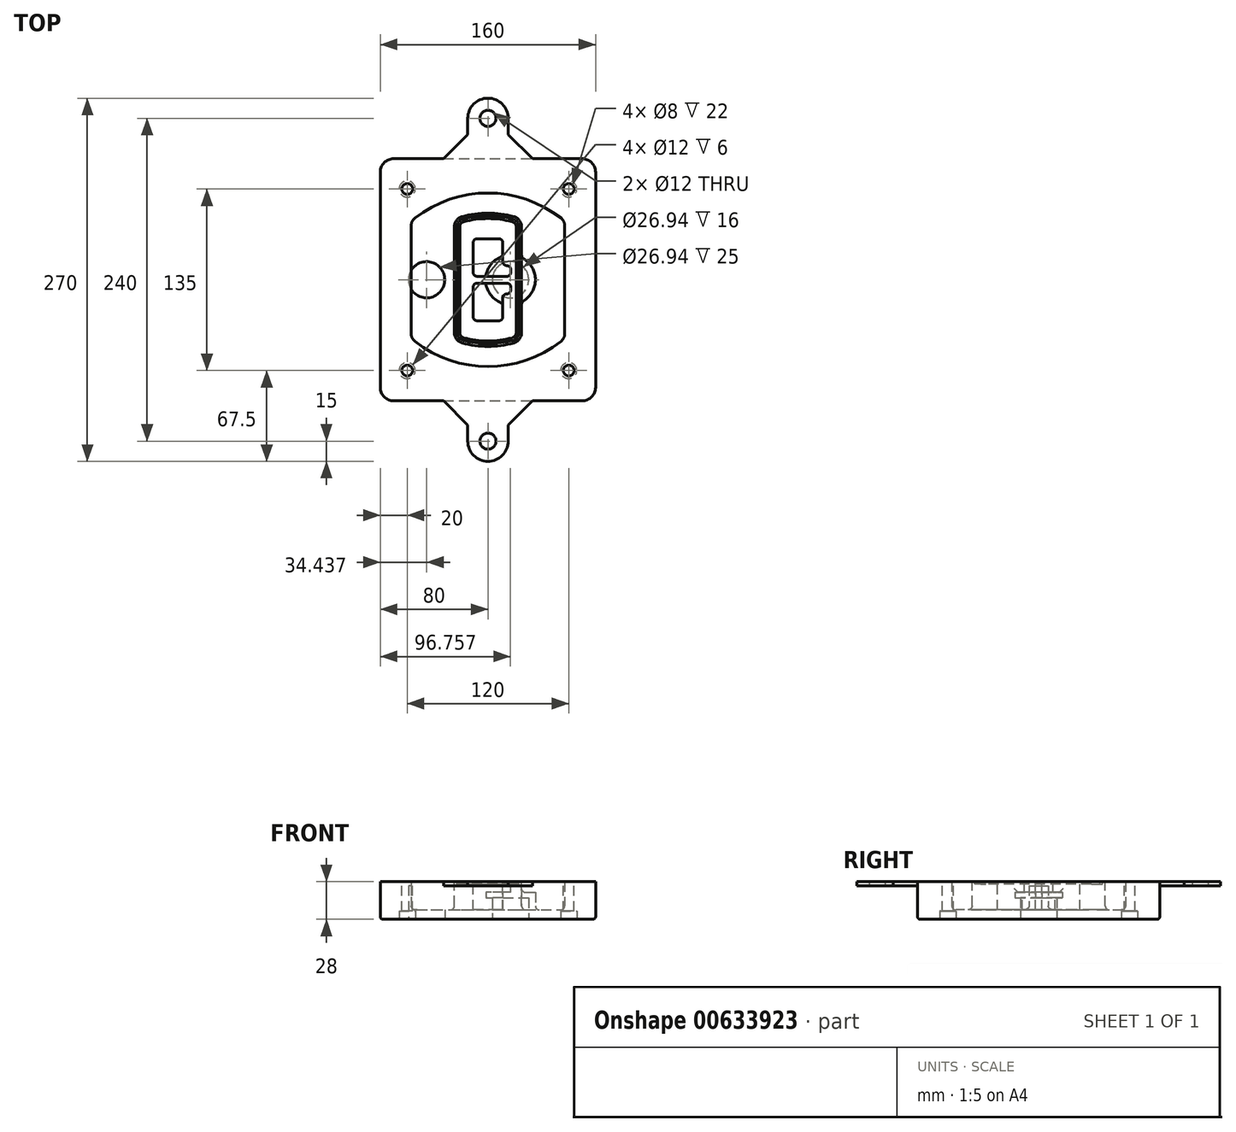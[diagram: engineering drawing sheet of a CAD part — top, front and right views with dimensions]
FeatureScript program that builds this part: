
annotation { "Feature Type Name" : "Feature", "Feature Type Description" : "" }
export const myFeature = defineFeature(function(context is Context, id is Id, definition is map)
    precondition{}
    {
        {
            var Q0;
            Q0=qCreatedBy(makeId("Top.planeOp"),FACE);
            var sketch = newSketch(context, id + "F0", { "sketchPlane" : qUnion([Q0])});
            skPoint(sketch, "E0.rect.middle", {"position": v(0, 0) * mm});
            skLineSegment(sketch, "E1.bottom", {"start": v(-70, -90) * mm, "end": v(70, -90) * mm});
            skLineSegment(sketch, "E1.top", {"start": v(-70, 90) * mm, "end": v(70, 90) * mm});
            skLineSegment(sketch, "E1.left", {"start": v(-80, -80) * mm, "end": v(-80, 80) * mm});
            skLineSegment(sketch, "E1.right", {"start": v(80, -80) * mm, "end": v(80, 80) * mm});
            skLineSegment(sketch, "E2", {"start": v(-80, 90) * mm, "end": v(80, -90) * mm, "construction": true});
            skLineSegment(sketch, "E3", {"start": v(80, 90) * mm, "end": v(-80, -90) * mm, "construction": true});
            skCircle(sketch, "E4", {"center": v(-60, 67.5) * mm, "radius": 4 * mm});
            skCircle(sketch, "E5", {"center": v(60, 67.5) * mm, "radius": 4 * mm});
            skCircle(sketch, "E6", {"center": v(60, -67.5) * mm, "radius": 4 * mm});
            skCircle(sketch, "E7", {"center": v(-60, -67.5) * mm, "radius": 4 * mm});
            skLineSegment(sketch, "E8", {"start": v(-60, 67.5) * mm, "end": v(60, 67.5) * mm, "construction": true});
            skLineSegment(sketch, "E9", {"start": v(60, 67.5) * mm, "end": v(60, -67.5) * mm, "construction": true});
            skLineSegment(sketch, "E10", {"start": v(60, -67.5) * mm, "end": v(-60, -67.5) * mm, "construction": true});
            skLineSegment(sketch, "E11", {"start": v(-60, -67.5) * mm, "end": v(-60, 67.5) * mm, "construction": true});
            skLineSegment(sketch, "E12", {"start": v(-60, 40.3) * mm, "end": v(-60, -40.3) * mm});
            skLineSegment(sketch, "E13", {"start": v(60, 40.3) * mm, "end": v(60, -40.3) * mm});
            skArc(sketch, "E14", {"start": v(56.15, 48.18) * mm, "mid": v(0, 67.5) * mm, "end": v(-56.15, 48.18) * mm});
            skArc(sketch, "E15", {"start": v(-56.15, -48.18) * mm, "mid": v(0, -67.5) * mm, "end": v(56.15, -48.18) * mm});
            skLineSegment(sketch, "E16", {"start": v(-60, 0) * mm, "end": v(60, 0) * mm, "construction": true});
            skPoint(sketch, "E17.visualSharp", {"position": v(-60, -45) * mm});
            skArc(sketch, "E17.filletArc", {"start": v(-60, -40.3) * mm, "mid": v(-58.99, -44.68) * mm, "end": v(-56.15, -48.18) * mm});
            skPoint(sketch, "E18.visualSharp", {"position": v(-60, 45) * mm});
            skArc(sketch, "E18.filletArc", {"start": v(-56.15, 48.18) * mm, "mid": v(-58.99, 44.68) * mm, "end": v(-60, 40.3) * mm});
            skPoint(sketch, "E19.visualSharp", {"position": v(60, 45) * mm});
            skArc(sketch, "E19.filletArc", {"start": v(60, 40.3) * mm, "mid": v(58.99, 44.68) * mm, "end": v(56.15, 48.18) * mm});
            skPoint(sketch, "E20.visualSharp", {"position": v(60, -45) * mm});
            skArc(sketch, "E20.filletArc", {"start": v(56.15, -48.18) * mm, "mid": v(58.99, -44.68) * mm, "end": v(60, -40.3) * mm});
            skPoint(sketch, "E21.visualSharp", {"position": v(-80, 90) * mm});
            skArc(sketch, "E21.filletArc", {"start": v(-70, 90) * mm, "mid": v(-77.07, 87.07) * mm, "end": v(-80, 80) * mm});
            skPoint(sketch, "E22.visualSharp", {"position": v(80, 90) * mm});
            skArc(sketch, "E22.filletArc", {"start": v(80, 80) * mm, "mid": v(77.07, 87.07) * mm, "end": v(70, 90) * mm});
            skPoint(sketch, "E23.visualSharp", {"position": v(80, -90) * mm});
            skArc(sketch, "E23.filletArc", {"start": v(70, -90) * mm, "mid": v(77.07, -87.07) * mm, "end": v(80, -80) * mm});
            skPoint(sketch, "E24.visualSharp", {"position": v(-80, -90) * mm});
            skArc(sketch, "E24.filletArc", {"start": v(-80, -80) * mm, "mid": v(-77.07, -87.07) * mm, "end": v(-70, -90) * mm});
            skArc(sketch, "E25.0", {"start": v(57, 40.3) * mm, "mid": v(56.3, 43.36) * mm, "end": v(54.3, 45.81) * mm});
            skLineSegment(sketch, "E25.1", {"start": v(57, 40.3) * mm, "end": v(57, -40.3) * mm});
            skArc(sketch, "E25.2", {"start": v(54.3, -45.81) * mm, "mid": v(56.3, -43.36) * mm, "end": v(57, -40.3) * mm});
            skArc(sketch, "E25.3", {"start": v(-54.3, -45.81) * mm, "mid": v(0, -64.5) * mm, "end": v(54.3, -45.81) * mm});
            skArc(sketch, "E25.4", {"start": v(-57, -40.3) * mm, "mid": v(-56.3, -43.36) * mm, "end": v(-54.3, -45.81) * mm});
            skArc(sketch, "E25.5", {"start": v(54.3, 45.81) * mm, "mid": v(0, 64.5) * mm, "end": v(-54.3, 45.81) * mm});
            skLineSegment(sketch, "E25.6", {"start": v(-57, 40.3) * mm, "end": v(-57, -40.3) * mm});
            skArc(sketch, "E25.7", {"start": v(-54.3, 45.81) * mm, "mid": v(-56.3, 43.36) * mm, "end": v(-57, 40.3) * mm});
            skArc(sketch, "E26.0", {"start": v(-58.62, 51.33) * mm, "mid": v(-62.58, 46.43) * mm, "end": v(-64, 40.3) * mm});
            skArc(sketch, "E26.1", {"start": v(58.62, 51.33) * mm, "mid": v(0, 71.5) * mm, "end": v(-58.62, 51.33) * mm});
            skArc(sketch, "E26.2", {"start": v(64, 40.3) * mm, "mid": v(62.58, 46.43) * mm, "end": v(58.62, 51.33) * mm});
            skLineSegment(sketch, "E26.3", {"start": v(64, 40.3) * mm, "end": v(64, -40.3) * mm});
            skArc(sketch, "E26.4", {"start": v(58.62, -51.33) * mm, "mid": v(62.58, -46.43) * mm, "end": v(64, -40.3) * mm});
            skLineSegment(sketch, "E26.5", {"start": v(-64, 40.3) * mm, "end": v(-64, -40.3) * mm});
            skArc(sketch, "E26.6", {"start": v(-58.62, -51.33) * mm, "mid": v(0, -71.5) * mm, "end": v(58.62, -51.33) * mm});
            skArc(sketch, "E26.7", {"start": v(-64, -40.3) * mm, "mid": v(-62.58, -46.43) * mm, "end": v(-58.62, -51.33) * mm});
            skSolve(sketch);
        }
        {
            var Q0;
            Q0=makeQuery(id+"F0.imprint","IMPRINT",FACE,{"disambiguationData":[TD([[makeQuery(id+"F0.imprint","IMPRINT",EDGE,{"derivedFrom":sQuery(id+"F0.wireOp",EDGE,"E1.bottom")}),1.0]])]});
            var Q1;
            Q1=makeQuery(id+"F0.imprint","IMPRINT",FACE,{"disambiguationData":[TD([[makeQuery(id+"F0.imprint","IMPRINT",EDGE,{"derivedFrom":sQuery(id+"F0.wireOp",EDGE,"E12")}),1.0]])]});
            var Q2;
            Q2=makeQuery(id+"F0.imprint","IMPRINT",FACE,{"disambiguationData":[TD([[makeQuery(id+"F0.imprint","IMPRINT",EDGE,{"derivedFrom":sQuery(id+"F0.wireOp",EDGE,"E25.0")}),1.0]])]});
            var Q3;
            Q3=makeQuery(id+"F0.imprint","IMPRINT",FACE,{"disambiguationData":[TD([[makeQuery(id+"F0.imprint","IMPRINT",EDGE,{"derivedFrom":sQuery(id+"F0.wireOp",EDGE,"E12")}),-1.0]])]});
            extrude(context, id + "F1", {"entities" : qUnion([Q0, Q1, Q2, Q3]), "oppositeDirection" : true, "depth" : 25 * mm});
        }
        {
            var Q0;
            Q0=makeQuery(id+"F0.imprint","IMPRINT",FACE,{"disambiguationData":[TD([[makeQuery(id+"F0.imprint","IMPRINT",EDGE,{"derivedFrom":sQuery(id+"F0.wireOp",EDGE,"E12")}),1.0]])]});
            extrude(context, id + "F2", {"entities" : qUnion([Q0]), "operationType" : NewBodyOperationType.ADD, "depth" : 3 * mm});
        }
        {
            var Q0;
            Q0=makeQuery(id+"F0.imprint","IMPRINT",FACE,{"disambiguationData":[TD([[makeQuery(id+"F0.imprint","IMPRINT",EDGE,{"derivedFrom":sQuery(id+"F0.wireOp",EDGE,"E25.0")}),1.0]])]});
            extrude(context, id + "F3", {"entities" : qUnion([Q0]), "operationType" : NewBodyOperationType.REMOVE, "oppositeDirection" : true, "depth" : 18 * mm});
        }
        {
            var Q0;
            Q0=makeQuery(id+"F2.opExtrude","CAP_FACE",FACE,{"disambiguationData":[OSD([sQuery(id+"F0.wireOp",EDGE,"E12"),sQuery(id+"F0.wireOp",EDGE,"E13"),sQuery(id+"F0.wireOp",EDGE,"E14"),sQuery(id+"F0.wireOp",EDGE,"E15"),sQuery(id+"F0.wireOp",EDGE,"E17.filletArc"),sQuery(id+"F0.wireOp",EDGE,"E18.filletArc"),sQuery(id+"F0.wireOp",EDGE,"E19.filletArc"),sQuery(id+"F0.wireOp",EDGE,"E20.filletArc"),sQuery(id+"F0.wireOp",EDGE,"E25.0"),sQuery(id+"F0.wireOp",EDGE,"E25.1"),sQuery(id+"F0.wireOp",EDGE,"E25.2"),sQuery(id+"F0.wireOp",EDGE,"E25.3"),sQuery(id+"F0.wireOp",EDGE,"E25.4"),sQuery(id+"F0.wireOp",EDGE,"E25.5"),sQuery(id+"F0.wireOp",EDGE,"E25.6"),sQuery(id+"F0.wireOp",EDGE,"E25.7")])],"isStart":false});
            var sketch = newSketch(context, id + "F4", { "sketchPlane" : qUnion([Q0])});
            skArc(sketch, "E27.0", {"start": v(-19.08, -46.97) * mm, "mid": v(0, -49.5) * mm, "end": v(19.08, -46.97) * mm});
            skArc(sketch, "E28.0", {"start": v(19.08, 46.97) * mm, "mid": v(0, 49.5) * mm, "end": v(-19.08, 46.97) * mm});
            skLineSegment(sketch, "E29", {"start": v(-25, 39.25) * mm, "end": v(-25, -39.25) * mm});
            skLineSegment(sketch, "E30", {"start": v(25, 39.25) * mm, "end": v(25, -39.25) * mm});
            skLineSegment(sketch, "E31", {"start": v(-25, 45.1) * mm, "end": v(25, 45.1) * mm, "construction": true});
            skLineSegment(sketch, "E32", {"start": v(-25, -45.1) * mm, "end": v(25, -45.1) * mm, "construction": true});
            skPoint(sketch, "E33.visualSharp", {"position": v(-25, 45.1) * mm});
            skArc(sketch, "E33.filletArc", {"start": v(-19.08, 46.97) * mm, "mid": v(-23.35, 44.11) * mm, "end": v(-25, 39.25) * mm});
            skPoint(sketch, "E34.visualSharp", {"position": v(25, 45.1) * mm});
            skArc(sketch, "E34.filletArc", {"start": v(25, 39.25) * mm, "mid": v(23.35, 44.11) * mm, "end": v(19.08, 46.97) * mm});
            skPoint(sketch, "E35.visualSharp", {"position": v(25, -45.1) * mm});
            skArc(sketch, "E35.filletArc", {"start": v(19.08, -46.97) * mm, "mid": v(23.35, -44.11) * mm, "end": v(25, -39.25) * mm});
            skPoint(sketch, "E36.visualSharp", {"position": v(-25, -45.1) * mm});
            skArc(sketch, "E36.filletArc", {"start": v(-25, -39.25) * mm, "mid": v(-23.35, -44.11) * mm, "end": v(-19.08, -46.97) * mm});
            skArc(sketch, "E37.0", {"start": v(54.3, 45.81) * mm, "mid": v(0, 64.5) * mm, "end": v(-54.3, 45.81) * mm});
            skArc(sketch, "E37.1", {"start": v(-54.3, 45.81) * mm, "mid": v(-56.3, 43.36) * mm, "end": v(-57, 40.3) * mm});
            skLineSegment(sketch, "E37.2", {"start": v(-57, 40.3) * mm, "end": v(-57, -40.3) * mm});
            skArc(sketch, "E37.3", {"start": v(-57, -40.3) * mm, "mid": v(-56.3, -43.36) * mm, "end": v(-54.3, -45.81) * mm});
            skArc(sketch, "E37.4", {"start": v(-54.3, -45.81) * mm, "mid": v(0, -64.5) * mm, "end": v(54.3, -45.81) * mm});
            skArc(sketch, "E37.5", {"start": v(54.3, -45.81) * mm, "mid": v(56.3, -43.36) * mm, "end": v(57, -40.3) * mm});
            skLineSegment(sketch, "E37.6", {"start": v(57, 40.3) * mm, "end": v(57, -40.3) * mm});
            skArc(sketch, "E37.7", {"start": v(57, 40.3) * mm, "mid": v(56.3, 43.36) * mm, "end": v(54.3, 45.81) * mm});
            skLineSegment(sketch, "E38.0", {"start": v(23, 39.25) * mm, "end": v(23, -39.25) * mm});
            skArc(sketch, "E38.1", {"start": v(18.56, -45.04) * mm, "mid": v(21.76, -42.9) * mm, "end": v(23, -39.25) * mm});
            skArc(sketch, "E38.2", {"start": v(-18.56, -45.04) * mm, "mid": v(0, -47.5) * mm, "end": v(18.56, -45.04) * mm});
            skArc(sketch, "E38.3", {"start": v(-23, -39.25) * mm, "mid": v(-21.76, -42.9) * mm, "end": v(-18.56, -45.04) * mm});
            skLineSegment(sketch, "E38.4", {"start": v(-23, 39.25) * mm, "end": v(-23, -39.25) * mm});
            skArc(sketch, "E38.5", {"start": v(23, 39.25) * mm, "mid": v(21.76, 42.9) * mm, "end": v(18.56, 45.04) * mm});
            skArc(sketch, "E38.6", {"start": v(-18.56, 45.04) * mm, "mid": v(-21.76, 42.9) * mm, "end": v(-23, 39.25) * mm});
            skArc(sketch, "E38.7", {"start": v(18.56, 45.04) * mm, "mid": v(0, 47.5) * mm, "end": v(-18.56, 45.04) * mm});
            skArc(sketch, "E39.0", {"start": v(21, 39.25) * mm, "mid": v(20.18, 41.68) * mm, "end": v(18.04, 43.1) * mm});
            skLineSegment(sketch, "E39.1", {"start": v(21, 39.25) * mm, "end": v(21, -39.25) * mm});
            skArc(sketch, "E39.2", {"start": v(18.04, -43.1) * mm, "mid": v(20.18, -41.68) * mm, "end": v(21, -39.25) * mm});
            skArc(sketch, "E39.3", {"start": v(-18.04, -43.1) * mm, "mid": v(0, -45.5) * mm, "end": v(18.04, -43.1) * mm});
            skArc(sketch, "E39.4", {"start": v(-21, -39.25) * mm, "mid": v(-20.18, -41.68) * mm, "end": v(-18.04, -43.1) * mm});
            skArc(sketch, "E39.5", {"start": v(18.04, 43.1) * mm, "mid": v(0, 45.5) * mm, "end": v(-18.04, 43.1) * mm});
            skLineSegment(sketch, "E39.6", {"start": v(-21, 39.25) * mm, "end": v(-21, -39.25) * mm});
            skArc(sketch, "E39.7", {"start": v(-18.04, 43.1) * mm, "mid": v(-20.18, 41.68) * mm, "end": v(-21, 39.25) * mm});
            skLineSegment(sketch, "E40", {"start": v(-25, 0) * mm, "end": v(25, 0) * mm, "construction": true});
            skLineSegment(sketch, "E41", {"start": v(-11, 5.5) * mm, "end": v(-11, 27.5) * mm});
            skLineSegment(sketch, "E42", {"start": v(-8, 30.5) * mm, "end": v(8, 30.5) * mm});
            skLineSegment(sketch, "E43", {"start": v(11, 27.5) * mm, "end": v(11, 13.5) * mm});
            skLineSegment(sketch, "E44", {"start": v(14, 10.5) * mm, "end": v(14, 10.5) * mm});
            skLineSegment(sketch, "E45", {"start": v(17, 7.5) * mm, "end": v(17, 5.5) * mm});
            skLineSegment(sketch, "E46", {"start": v(14, 2.5) * mm, "end": v(-8, 2.5) * mm});
            skPoint(sketch, "E47.visualSharp", {"position": v(-11, 30.5) * mm});
            skArc(sketch, "E47.filletArc", {"start": v(-8, 30.5) * mm, "mid": v(-10.12, 29.62) * mm, "end": v(-11, 27.5) * mm});
            skPoint(sketch, "E48.visualSharp", {"position": v(11, 30.5) * mm});
            skArc(sketch, "E48.filletArc", {"start": v(11, 27.5) * mm, "mid": v(10.12, 29.62) * mm, "end": v(8, 30.5) * mm});
            skPoint(sketch, "E49.visualSharp", {"position": v(11, 10.5) * mm});
            skArc(sketch, "E49.filletArc", {"start": v(11, 13.5) * mm, "mid": v(11.88, 11.38) * mm, "end": v(14, 10.5) * mm});
            skPoint(sketch, "E50.visualSharp", {"position": v(17, 10.5) * mm});
            skArc(sketch, "E50.filletArc", {"start": v(17, 7.5) * mm, "mid": v(16.12, 9.62) * mm, "end": v(14, 10.5) * mm});
            skPoint(sketch, "E51.visualSharp", {"position": v(17, 2.5) * mm});
            skArc(sketch, "E51.filletArc", {"start": v(14, 2.5) * mm, "mid": v(16.12, 3.38) * mm, "end": v(17, 5.5) * mm});
            skPoint(sketch, "E52.visualSharp", {"position": v(-11, 2.5) * mm});
            skArc(sketch, "E52.filletArc", {"start": v(-11, 5.5) * mm, "mid": v(-10.12, 3.38) * mm, "end": v(-8, 2.5) * mm});
            skLineSegment(sketch, "E53.0.MirrorCS", {"start": v(14, -2.5) * mm, "end": v(-8, -2.5) * mm});
            skArc(sketch, "E54.0.MirrorCS", {"start": v(-11, -5.5) * mm, "mid": v(-10.12, -3.38) * mm, "end": v(-8, -2.5) * mm});
            skLineSegment(sketch, "E55.0.MirrorCS", {"start": v(-11, -5.5) * mm, "end": v(-11, -27.5) * mm});
            skArc(sketch, "E56.0.MirrorCS", {"start": v(-8, -30.5) * mm, "mid": v(-10.12, -29.62) * mm, "end": v(-11, -27.5) * mm});
            skLineSegment(sketch, "E57.0.MirrorCS", {"start": v(-8, -30.5) * mm, "end": v(8, -30.5) * mm});
            skArc(sketch, "E58.0.MirrorCS", {"start": v(11, -27.5) * mm, "mid": v(10.12, -29.62) * mm, "end": v(8, -30.5) * mm});
            skLineSegment(sketch, "E59.0.MirrorCS", {"start": v(11, -27.5) * mm, "end": v(11, -13.5) * mm});
            skArc(sketch, "E60.0.MirrorCS", {"start": v(11, -13.5) * mm, "mid": v(11.88, -11.38) * mm, "end": v(14, -10.5) * mm});
            skArc(sketch, "E61.0.MirrorCS", {"start": v(17, -7.5) * mm, "mid": v(16.12, -9.62) * mm, "end": v(14, -10.5) * mm});
            skLineSegment(sketch, "E62.0.MirrorCS", {"start": v(17, -7.5) * mm, "end": v(17, -5.5) * mm});
            skArc(sketch, "E63.0.MirrorCS", {"start": v(14, -2.5) * mm, "mid": v(16.12, -3.38) * mm, "end": v(17, -5.5) * mm});
            skSolve(sketch);
        }
        {
            var Q0;
            Q0=makeQuery(id+"F4.imprint","IMPRINT",FACE,{"disambiguationData":[TD([[makeQuery(id+"F4.imprint","IMPRINT",EDGE,{"derivedFrom":sQuery(id+"F4.wireOp",EDGE,"E27.0")}),1.0]])]});
            var Q1;
            Q1=makeQuery(id+"F4.imprint","IMPRINT",FACE,{"disambiguationData":[TD([[makeQuery(id+"F4.imprint","IMPRINT",EDGE,{"derivedFrom":sQuery(id+"F4.wireOp",EDGE,"E38.0")}),-1.0]])]});
            var Q2;
            Q2=makeQuery(id+"F4.imprint","IMPRINT",FACE,{"disambiguationData":[TD([[makeQuery(id+"F4.imprint","IMPRINT",EDGE,{"derivedFrom":sQuery(id+"F4.wireOp",EDGE,"E39.0")}),1.0]])]});
            extrude(context, id + "F5", {"entities" : qUnion([Q0, Q1, Q2]), "operationType" : NewBodyOperationType.ADD, "endBound" : BoundingType.UP_TO_NEXT, "oppositeDirection" : true, "depth" : 25 * mm});
        }
        {
            var Q0;
            Q0=makeQuery(id+"F4.imprint","IMPRINT",FACE,{"disambiguationData":[TD([[makeQuery(id+"F4.imprint","IMPRINT",EDGE,{"derivedFrom":sQuery(id+"F4.wireOp",EDGE,"E38.0")}),-1.0]])]});
            extrude(context, id + "F6", {"entities" : qUnion([Q0]), "operationType" : NewBodyOperationType.REMOVE, "oppositeDirection" : true, "depth" : 2 * mm});
        }
        {
            var Q0;
            Q0=makeQuery(id+"F1.opExtrude","CAP_FACE",FACE,{"disambiguationData":[OSD([sQuery(id+"F0.wireOp",EDGE,"E1.bottom"),sQuery(id+"F0.wireOp",EDGE,"E1.top"),sQuery(id+"F0.wireOp",EDGE,"E1.left"),sQuery(id+"F0.wireOp",EDGE,"E1.right"),sQuery(id+"F0.wireOp",EDGE,"E4"),sQuery(id+"F0.wireOp",EDGE,"E5"),sQuery(id+"F0.wireOp",EDGE,"E6"),sQuery(id+"F0.wireOp",EDGE,"E7"),sQuery(id+"F0.wireOp",EDGE,"E21.filletArc"),sQuery(id+"F0.wireOp",EDGE,"E22.filletArc"),sQuery(id+"F0.wireOp",EDGE,"E23.filletArc"),sQuery(id+"F0.wireOp",EDGE,"E24.filletArc")])],"isStart":false});
            var sketch = newSketch(context, id + "F7", { "sketchPlane" : qUnion([Q0])});
            skCircle(sketch, "E64", {"center": v(16.76, 0) * mm, "radius": 13.47 * mm});
            skCircle(sketch, "E65", {"center": v(-45.56, 0) * mm, "radius": 13.47 * mm});
            skLineSegment(sketch, "E66", {"start": v(80, 0) * mm, "end": v(-80, 0) * mm});
            skCircle(sketch, "E67", {"center": v(16.76, 0) * mm, "radius": 18.47 * mm});
            skCircle(sketch, "E68", {"center": v(60, -67.5) * mm, "radius": 6 * mm});
            skCircle(sketch, "E69", {"center": v(-60, -67.5) * mm, "radius": 6 * mm});
            skCircle(sketch, "E70", {"center": v(-60, 67.5) * mm, "radius": 6 * mm});
            skCircle(sketch, "E71", {"center": v(60, 67.5) * mm, "radius": 6 * mm});
            skSolve(sketch);
        }
        {
            var Q0;
            {var subQ1=sQuery(id+"F7.wireOp",EDGE,"E66");var subQ4=sQuery(id+"F7.wireOp",EDGE,"E64");var subQ6=makeQuery(id+"F7.imprint","INTERSECT",VERTEX,{"disambiguationData":[OD(0.0)],"derivedFrom":[subQ4,subQ1]});Q0=makeQuery(id+"F7.imprint","IMPRINT",FACE,{"disambiguationData":[TD([[makeQuery(id+"F7.imprint","IMPRINT",EDGE,{"disambiguationData":[TD([[subQ6,-1.0]])],"derivedFrom":subQ4}),-1.0]])]});}
            var Q1;
            {var subQ0=sQuery(id+"F7.wireOp",EDGE,"E66");var subQ1=sQuery(id+"F7.wireOp",EDGE,"E64");var subQ3=makeQuery(id+"F7.imprint","INTERSECT",VERTEX,{"disambiguationData":[OD(0.0)],"derivedFrom":[subQ1,subQ0]});Q1=makeQuery(id+"F7.imprint","IMPRINT",FACE,{"disambiguationData":[TD([[makeQuery(id+"F7.imprint","IMPRINT",EDGE,{"disambiguationData":[TD([[subQ3,-1.0]])],"derivedFrom":subQ1}),1.0]])]});}
            var Q2;
            {var subQ0=sQuery(id+"F7.wireOp",EDGE,"E66");var subQ1=sQuery(id+"F7.wireOp",EDGE,"E64");var subQ3=makeQuery(id+"F7.imprint","INTERSECT",VERTEX,{"disambiguationData":[OD(0.0)],"derivedFrom":[subQ1,subQ0]});Q2=makeQuery(id+"F7.imprint","IMPRINT",FACE,{"disambiguationData":[TD([[makeQuery(id+"F7.imprint","IMPRINT",EDGE,{"disambiguationData":[TD([[subQ3,1.0]])],"derivedFrom":subQ1}),1.0]])]});}
            var Q3;
            {var subQ1=sQuery(id+"F7.wireOp",EDGE,"E66");var subQ4=sQuery(id+"F7.wireOp",EDGE,"E64");var subQ6=makeQuery(id+"F7.imprint","INTERSECT",VERTEX,{"disambiguationData":[OD(0.0)],"derivedFrom":[subQ4,subQ1]});Q3=makeQuery(id+"F7.imprint","IMPRINT",FACE,{"disambiguationData":[TD([[makeQuery(id+"F7.imprint","IMPRINT",EDGE,{"disambiguationData":[TD([[subQ6,1.0]])],"derivedFrom":subQ4}),-1.0]])]});}
            extrude(context, id + "F8", {"entities" : qUnion([Q0, Q1, Q2, Q3]), "operationType" : NewBodyOperationType.ADD, "oppositeDirection" : true, "depth" : 20 * mm});
        }
        {
            var Q0;
            {var subQ0=sQuery(id+"F7.wireOp",EDGE,"E66");var subQ1=sQuery(id+"F7.wireOp",EDGE,"E64");var subQ3=makeQuery(id+"F7.imprint","INTERSECT",VERTEX,{"disambiguationData":[OD(0.0)],"derivedFrom":[subQ1,subQ0]});Q0=makeQuery(id+"F7.imprint","IMPRINT",FACE,{"disambiguationData":[TD([[makeQuery(id+"F7.imprint","IMPRINT",EDGE,{"disambiguationData":[TD([[subQ3,-1.0]])],"derivedFrom":subQ1}),1.0]])]});}
            var Q1;
            {var subQ0=sQuery(id+"F7.wireOp",EDGE,"E66");var subQ1=sQuery(id+"F7.wireOp",EDGE,"E64");var subQ3=makeQuery(id+"F7.imprint","INTERSECT",VERTEX,{"disambiguationData":[OD(0.0)],"derivedFrom":[subQ1,subQ0]});Q1=makeQuery(id+"F7.imprint","IMPRINT",FACE,{"disambiguationData":[TD([[makeQuery(id+"F7.imprint","IMPRINT",EDGE,{"disambiguationData":[TD([[subQ3,1.0]])],"derivedFrom":subQ1}),1.0]])]});}
            extrude(context, id + "F9", {"entities" : qUnion([Q0, Q1]), "operationType" : NewBodyOperationType.REMOVE, "oppositeDirection" : true, "depth" : 16 * mm});
        }
        {
            var Q0;
            {var subQ0=sQuery(id+"F7.wireOp",EDGE,"E66");var subQ1=sQuery(id+"F7.wireOp",EDGE,"E65");var subQ3=makeQuery(id+"F7.imprint","INTERSECT",VERTEX,{"disambiguationData":[OD(0.0)],"derivedFrom":[subQ1,subQ0]});Q0=makeQuery(id+"F7.imprint","IMPRINT",FACE,{"disambiguationData":[TD([[makeQuery(id+"F7.imprint","IMPRINT",EDGE,{"disambiguationData":[TD([[subQ3,-1.0]])],"derivedFrom":subQ1}),1.0]])]});}
            var Q1;
            {var subQ0=sQuery(id+"F7.wireOp",EDGE,"E66");var subQ1=sQuery(id+"F7.wireOp",EDGE,"E65");var subQ3=makeQuery(id+"F7.imprint","INTERSECT",VERTEX,{"disambiguationData":[OD(0.0)],"derivedFrom":[subQ1,subQ0]});Q1=makeQuery(id+"F7.imprint","IMPRINT",FACE,{"disambiguationData":[TD([[makeQuery(id+"F7.imprint","IMPRINT",EDGE,{"disambiguationData":[TD([[subQ3,1.0]])],"derivedFrom":subQ1}),1.0]])]});}
            extrude(context, id + "F10", {"entities" : qUnion([Q0, Q1]), "operationType" : NewBodyOperationType.REMOVE, "oppositeDirection" : true, "depth" : 25 * mm});
        }
        {
            var Q0;
            Q0=makeQuery(id+"F7.imprint","IMPRINT",FACE,{"disambiguationData":[TD([[makeQuery(id+"F7.imprint","IMPRINT",EDGE,{"derivedFrom":sQuery(id+"F7.wireOp",EDGE,"E68")}),1.0]])]});
            var Q1;
            Q1=makeQuery(id+"F7.imprint","IMPRINT",FACE,{"disambiguationData":[TD([[makeQuery(id+"F7.imprint","IMPRINT",EDGE,{"derivedFrom":makeQuery(id+"F1.opExtrude","CAP_EDGE",EDGE,{"disambiguationData":[OSD([sQuery(id+"F0.wireOp",EDGE,"E5")])],"isStart":false})}),-1.0]])]});
            var Q2;
            Q2=makeQuery(id+"F7.imprint","IMPRINT",FACE,{"disambiguationData":[TD([[makeQuery(id+"F7.imprint","IMPRINT",EDGE,{"derivedFrom":sQuery(id+"F7.wireOp",EDGE,"E69")}),1.0]])]});
            var Q3;
            Q3=makeQuery(id+"F7.imprint","IMPRINT",FACE,{"disambiguationData":[TD([[makeQuery(id+"F7.imprint","IMPRINT",EDGE,{"derivedFrom":makeQuery(id+"F1.opExtrude","CAP_EDGE",EDGE,{"disambiguationData":[OSD([sQuery(id+"F0.wireOp",EDGE,"E4")])],"isStart":false})}),-1.0]])]});
            var Q4;
            Q4=makeQuery(id+"F7.imprint","IMPRINT",FACE,{"disambiguationData":[TD([[makeQuery(id+"F7.imprint","IMPRINT",EDGE,{"derivedFrom":sQuery(id+"F7.wireOp",EDGE,"E70")}),1.0]])]});
            var Q5;
            Q5=makeQuery(id+"F7.imprint","IMPRINT",FACE,{"disambiguationData":[TD([[makeQuery(id+"F7.imprint","IMPRINT",EDGE,{"derivedFrom":makeQuery(id+"F1.opExtrude","CAP_EDGE",EDGE,{"disambiguationData":[OSD([sQuery(id+"F0.wireOp",EDGE,"E7")])],"isStart":false})}),-1.0]])]});
            var Q6;
            Q6=makeQuery(id+"F7.imprint","IMPRINT",FACE,{"disambiguationData":[TD([[makeQuery(id+"F7.imprint","IMPRINT",EDGE,{"derivedFrom":sQuery(id+"F7.wireOp",EDGE,"E71")}),1.0]])]});
            var Q7;
            Q7=makeQuery(id+"F7.imprint","IMPRINT",FACE,{"disambiguationData":[TD([[makeQuery(id+"F7.imprint","IMPRINT",EDGE,{"derivedFrom":makeQuery(id+"F1.opExtrude","CAP_EDGE",EDGE,{"disambiguationData":[OSD([sQuery(id+"F0.wireOp",EDGE,"E6")])],"isStart":false})}),-1.0]])]});
            extrude(context, id + "F11", {"entities" : qUnion([Q0, Q1, Q2, Q3, Q4, Q5, Q6, Q7]), "operationType" : NewBodyOperationType.REMOVE, "oppositeDirection" : true, "depth" : 6 * mm});
        }
        {
            var Q0;
            Q0=makeQuery(id+"F9.boolean.opBoolean","COPY",FACE,{"derivedFrom":makeQuery(id+"F9.opExtrude","CAP_FACE",FACE,{"disambiguationData":[OSD([sQuery(id+"F7.wireOp",EDGE,"E64")])],"isStart":false})});
            var sketch = newSketch(context, id + "F12", { "sketchPlane" : qUnion([Q0])});
            skArc(sketch, "E72.0", {"start": v(11, 17.55) * mm, "mid": v(2.57, 11.82) * mm, "end": v(-1.54, 2.5) * mm});
            skArc(sketch, "E72.1", {"start": v(-1.54, -2.5) * mm, "mid": v(2.57, -11.82) * mm, "end": v(11, -17.55) * mm});
            skLineSegment(sketch, "E73", {"start": v(-1.54, -2.5) * mm, "end": v(14, -2.5) * mm});
            skLineSegment(sketch, "E74.0", {"start": v(14, 2.5) * mm, "end": v(-1.54, 2.5) * mm});
            skArc(sketch, "E74.1", {"start": v(14, 2.5) * mm, "mid": v(16.12, 3.38) * mm, "end": v(17, 5.5) * mm});
            skLineSegment(sketch, "E74.2", {"start": v(17, 7.5) * mm, "end": v(17, 5.5) * mm});
            skArc(sketch, "E74.3", {"start": v(17, 7.5) * mm, "mid": v(16.12, 9.62) * mm, "end": v(14, 10.5) * mm});
            skArc(sketch, "E74.4", {"start": v(11, 13.5) * mm, "mid": v(11.88, 11.38) * mm, "end": v(14, 10.5) * mm});
            skLineSegment(sketch, "E74.5", {"start": v(11, 17.55) * mm, "end": v(11, 13.5) * mm});
            skLineSegment(sketch, "E74.7", {"start": v(14, -2.5) * mm, "end": v(-1.54, -2.5) * mm});
            skArc(sketch, "E74.8", {"start": v(14, -2.5) * mm, "mid": v(16.12, -3.38) * mm, "end": v(17, -5.5) * mm});
            skLineSegment(sketch, "E74.9", {"start": v(17, -7.5) * mm, "end": v(17, -5.5) * mm});
            skArc(sketch, "E74.10", {"start": v(17, -7.5) * mm, "mid": v(16.12, -9.62) * mm, "end": v(14, -10.5) * mm});
            skArc(sketch, "E74.11", {"start": v(11, -13.5) * mm, "mid": v(11.88, -11.38) * mm, "end": v(14, -10.5) * mm});
            skLineSegment(sketch, "E74.12", {"start": v(11, -17.55) * mm, "end": v(11, -13.5) * mm});
            skPoint(sketch, "E75.orphan", {"position": v(11, -27.5) * mm});
            skPoint(sketch, "E76.orphan", {"position": v(-8, -2.5) * mm});
            skPoint(sketch, "E77.orphan", {"position": v(-8, 2.5) * mm});
            skPoint(sketch, "E78.orphan", {"position": v(11, 27.5) * mm});
            skSolve(sketch);
        }
        {
            var Q0;
            {var subQ7=sQuery(id+"F12.wireOp",EDGE,"E72.0");var subQ14=sQuery(id+"F12.wireOp",EDGE,"E72.1");var subQ16=sQuery(id+"F12.wireOp",EDGE,"E74.1");var subQ18=sQuery(id+"F12.wireOp",EDGE,"E74.8");Q0=qUnion([makeQuery(id+"F12.imprint","IMPRINT",FACE,{"disambiguationData":[TD([[makeQuery(id+"F12.imprint","IMPRINT",EDGE,{"derivedFrom":subQ7}),1.0]])]}),makeQuery(id+"F12.imprint","IMPRINT",FACE,{"disambiguationData":[TD([[makeQuery(id+"F12.imprint","IMPRINT",EDGE,{"derivedFrom":subQ14}),1.0]])]}),makeQuery(id+"F12.imprint","IMPRINT",FACE,{"disambiguationData":[TD([[makeQuery(id+"F12.imprint","IMPRINT",EDGE,{"derivedFrom":subQ16}),1.0]])]}),makeQuery(id+"F12.imprint","IMPRINT",FACE,{"disambiguationData":[TD([[makeQuery(id+"F12.imprint","IMPRINT",EDGE,{"derivedFrom":subQ18}),-1.0]])]})]);}
            var Q1;
            Q1=makeQuery(id+"F5.boolean.opBoolean","SPLIT",FACE,{"disambiguationData":[TD([makeQuery(id+"F5.opExtrude","SWEPT_FACE",FACE,{"disambiguationData":[OSD([sQuery(id+"F4.wireOp",EDGE,"E41")])]})])],"derivedFrom":makeQuery(id+"F3.boolean.opBoolean","COPY",FACE,{"derivedFrom":makeQuery(id+"F3.opExtrude","CAP_FACE",FACE,{"disambiguationData":[OSD([sQuery(id+"F0.wireOp",EDGE,"E25.0"),sQuery(id+"F0.wireOp",EDGE,"E25.1"),sQuery(id+"F0.wireOp",EDGE,"E25.2"),sQuery(id+"F0.wireOp",EDGE,"E25.3"),sQuery(id+"F0.wireOp",EDGE,"E25.4"),sQuery(id+"F0.wireOp",EDGE,"E25.5"),sQuery(id+"F0.wireOp",EDGE,"E25.6"),sQuery(id+"F0.wireOp",EDGE,"E25.7")])],"isStart":false})})});
            extrude(context, id + "F13", {"entities" : qUnion([Q0]), "operationType" : NewBodyOperationType.REMOVE, "endBound" : BoundingType.UP_TO_SURFACE, "endBoundEntityFace" : qUnion([Q1]), "depth" : 25 * mm});
        }
        {
            var Q0;
            Q0=makeQuery(id+"F3.boolean.opBoolean","COPY",EDGE,{"derivedFrom":makeQuery(id+"F3.opExtrude","CAP_EDGE",EDGE,{"disambiguationData":[OSD([sQuery(id+"F0.wireOp",EDGE,"E25.6")])],"isStart":false})});
            var Q1;
            Q1=makeQuery(id+"F8.boolean.opBoolean","INTERSECT",EDGE,{"derivedFrom":[makeQuery(id+"F5.opExtrude","SWEPT_FACE",FACE,{"disambiguationData":[OSD([sQuery(id+"F4.wireOp",EDGE,"E30")])]}),makeQuery(id+"F8.opExtrude","CAP_FACE",FACE,{"disambiguationData":[OSD([sQuery(id+"F7.wireOp",EDGE,"E67")])],"isStart":false})]});
            var Q2;
            Q2=makeQuery(id+"F8.boolean.opBoolean","INTERSECT",EDGE,{"disambiguationData":[OD(1.0)],"derivedFrom":[makeQuery(id+"F5.opExtrude","SWEPT_FACE",FACE,{"disambiguationData":[OSD([sQuery(id+"F4.wireOp",EDGE,"E30")])]}),makeQuery(id+"F8.opExtrude","SWEPT_FACE",FACE,{"disambiguationData":[OSD([sQuery(id+"F7.wireOp",EDGE,"E67")])]})]});
            var Q3;
            {var subQ0=sQuery(id+"F4.wireOp",EDGE,"E30");Q3=makeQuery(id+"F8.boolean.opBoolean","SPLIT",EDGE,{"disambiguationData":[TD([makeQuery(id+"F5.opExtrude","SWEPT_FACE",FACE,{"disambiguationData":[OSD([sQuery(id+"F4.wireOp",EDGE,"E35.filletArc")])]})])],"derivedFrom":makeQuery(id+"F5.opExtrude","CAP_EDGE",EDGE,{"disambiguationData":[OSD([subQ0])],"isStart":false})});}
            var Q4;
            {var subQ0=sQuery(id+"F0.wireOp",EDGE,"E25.7");var subQ1=sQuery(id+"F0.wireOp",EDGE,"E25.1");var subQ2=sQuery(id+"F0.wireOp",EDGE,"E25.6");var subQ3=sQuery(id+"F0.wireOp",EDGE,"E25.5");var subQ4=sQuery(id+"F0.wireOp",EDGE,"E25.4");var subQ5=sQuery(id+"F0.wireOp",EDGE,"E25.0");var subQ6=sQuery(id+"F0.wireOp",EDGE,"E25.2");var subQ7=sQuery(id+"F0.wireOp",EDGE,"E25.3");Q4=makeQuery(id+"F8.boolean.opBoolean","INTERSECT",EDGE,{"derivedFrom":[makeQuery(id+"F5.boolean.opBoolean","SPLIT",FACE,{"disambiguationData":[TD([makeQuery(id+"F2.opExtrude","SWEPT_FACE",FACE,{"disambiguationData":[OSD([subQ5])]})])],"derivedFrom":makeQuery(id+"F3.boolean.opBoolean","COPY",FACE,{"derivedFrom":makeQuery(id+"F3.opExtrude","CAP_FACE",FACE,{"disambiguationData":[OSD([subQ5,subQ1,subQ6,subQ7,subQ4,subQ3,subQ2,subQ0])],"isStart":false})})}),makeQuery(id+"F8.opExtrude","SWEPT_FACE",FACE,{"disambiguationData":[OSD([sQuery(id+"F7.wireOp",EDGE,"E67")])]})]});}
            var Q5;
            Q5=makeQuery(id+"F8.boolean.opBoolean","INTERSECT",EDGE,{"disambiguationData":[OD(0.0)],"derivedFrom":[makeQuery(id+"F5.opExtrude","SWEPT_FACE",FACE,{"disambiguationData":[OSD([sQuery(id+"F4.wireOp",EDGE,"E30")])]}),makeQuery(id+"F8.opExtrude","SWEPT_FACE",FACE,{"disambiguationData":[OSD([sQuery(id+"F7.wireOp",EDGE,"E67")])]})]});
            fillet(context, id + "F14", {"entities" : qUnion([Q0, Q1, Q2, Q3, Q4, Q5]), "radius" : 3 * mm, "tangentPropagation" : true, "allowEdgeOverflow" : false});
        }
        {
            var Q0;
            Q0=makeQuery(id+"F1.opExtrude","CAP_EDGE",EDGE,{"disambiguationData":[OSD([sQuery(id+"F0.wireOp",EDGE,"E1.bottom")])],"isStart":false});
            fillet(context, id + "F15", {"entities" : qUnion([Q0]), "radius" : 2 * mm, "tangentPropagation" : true, "allowEdgeOverflow" : false});
        }
        {
            var Q0;
            {var subQ0=sQuery(id+"F0.wireOp",EDGE,"E21.filletArc");var subQ1=sQuery(id+"F0.wireOp",EDGE,"E7");var subQ2=sQuery(id+"F0.wireOp",EDGE,"E6");var subQ3=sQuery(id+"F0.wireOp",EDGE,"E5");var subQ4=sQuery(id+"F0.wireOp",EDGE,"E4");var subQ5=sQuery(id+"F0.wireOp",EDGE,"E22.filletArc");var subQ6=sQuery(id+"F0.wireOp",EDGE,"E1.bottom");var subQ7=sQuery(id+"F0.wireOp",EDGE,"E1.right");var subQ8=sQuery(id+"F0.wireOp",EDGE,"E1.top");var subQ9=sQuery(id+"F0.wireOp",EDGE,"E1.left");var subQ10=sQuery(id+"F0.wireOp",EDGE,"E23.filletArc");var subQ11=sQuery(id+"F0.wireOp",EDGE,"E24.filletArc");Q0=makeQuery(id+"F2.boolean.opBoolean","SPLIT",FACE,{"disambiguationData":[TD([makeQuery(id+"F1.opExtrude","SWEPT_FACE",FACE,{"disambiguationData":[OSD([subQ6])]})])],"derivedFrom":makeQuery(id+"F1.opExtrude","CAP_FACE",FACE,{"disambiguationData":[OSD([subQ6,subQ8,subQ9,subQ7,subQ4,subQ3,subQ2,subQ1,subQ0,subQ5,subQ10,subQ11])],"isStart":true})});}
            var sketch = newSketch(context, id + "F16", { "sketchPlane" : qUnion([Q0])});
            skLineSegment(sketch, "E79", {"start": v(0, 90) * mm, "end": v(0, 120) * mm, "construction": true});
            skLineSegment(sketch, "E80", {"start": v(-33, 90) * mm, "end": v(-15, 108) * mm});
            skLineSegment(sketch, "E81", {"start": v(-15, 108) * mm, "end": v(-15, 120) * mm});
            skLineSegment(sketch, "E82", {"start": v(33, 90) * mm, "end": v(15, 108) * mm});
            skLineSegment(sketch, "E83", {"start": v(15, 108) * mm, "end": v(15, 120) * mm});
            skArc(sketch, "E84", {"start": v(15, 120) * mm, "mid": v(0, 135) * mm, "end": v(-15, 120) * mm});
            skCircle(sketch, "E85", {"center": v(0, 120) * mm, "radius": 6 * mm});
            skLineSegment(sketch, "E86", {"start": v(-80, 0) * mm, "end": v(80, 0) * mm, "construction": true});
            skLineSegment(sketch, "E87.MirrorCS", {"start": v(33, -90) * mm, "end": v(15, -108) * mm});
            skArc(sketch, "E88.MirrorCS", {"start": v(15, -120) * mm, "mid": v(0, -135) * mm, "end": v(-15, -120) * mm});
            skLineSegment(sketch, "E89.MirrorCS", {"start": v(0, -90) * mm, "end": v(0, -120) * mm, "construction": true});
            skLineSegment(sketch, "E90.MirrorCS", {"start": v(-33, -90) * mm, "end": v(-15, -108) * mm});
            skLineSegment(sketch, "E91.MirrorCS", {"start": v(-15, -108) * mm, "end": v(-15, -120) * mm});
            skCircle(sketch, "E92.MirrorC", {"center": v(0, -120) * mm, "radius": 6 * mm});
            skLineSegment(sketch, "E93.MirrorCS", {"start": v(15, -108) * mm, "end": v(15, -120) * mm});
            skSolve(sketch);
        }
        {
            var Q0;
            {var subQ1=sQuery(id+"F16.wireOp",EDGE,"E87.MirrorCS");Q0=makeQuery(id+"F16.imprint","IMPRINT",FACE,{"disambiguationData":[TD([[makeQuery(id+"F16.imprint","IMPRINT",EDGE,{"derivedFrom":subQ1}),-1.0]])]});}
            var Q1;
            Q1=makeQuery(id+"F16.imprint","IMPRINT",FACE,{"disambiguationData":[TD([[makeQuery(id+"F16.imprint","IMPRINT",EDGE,{"derivedFrom":makeQuery(id+"F1.opExtrude","CAP_EDGE",EDGE,{"disambiguationData":[OSD([sQuery(id+"F0.wireOp",EDGE,"E1.left")])],"isStart":true})}),-1.0]])]});
            var Q2;
            {var subQ1=sQuery(id+"F16.wireOp",EDGE,"E80");Q2=makeQuery(id+"F16.imprint","IMPRINT",FACE,{"disambiguationData":[TD([[makeQuery(id+"F16.imprint","IMPRINT",EDGE,{"derivedFrom":subQ1}),-1.0]])]});}
            var Q3;
            Q3=makeQuery(id+"F2.opExtrude","CAP_FACE",FACE,{"disambiguationData":[OSD([sQuery(id+"F0.wireOp",EDGE,"E12"),sQuery(id+"F0.wireOp",EDGE,"E13"),sQuery(id+"F0.wireOp",EDGE,"E14"),sQuery(id+"F0.wireOp",EDGE,"E15"),sQuery(id+"F0.wireOp",EDGE,"E17.filletArc"),sQuery(id+"F0.wireOp",EDGE,"E18.filletArc"),sQuery(id+"F0.wireOp",EDGE,"E19.filletArc"),sQuery(id+"F0.wireOp",EDGE,"E20.filletArc"),sQuery(id+"F0.wireOp",EDGE,"E25.0"),sQuery(id+"F0.wireOp",EDGE,"E25.1"),sQuery(id+"F0.wireOp",EDGE,"E25.2"),sQuery(id+"F0.wireOp",EDGE,"E25.3"),sQuery(id+"F0.wireOp",EDGE,"E25.4"),sQuery(id+"F0.wireOp",EDGE,"E25.5"),sQuery(id+"F0.wireOp",EDGE,"E25.6"),sQuery(id+"F0.wireOp",EDGE,"E25.7")])],"isStart":false});
            extrude(context, id + "F17", {"entities" : qUnion([Q0, Q1, Q2]), "operationType" : NewBodyOperationType.ADD, "endBound" : BoundingType.UP_TO_SURFACE, "depth" : 25 * mm, "endBoundEntityFace" : qUnion([Q3]), "offsetDistance" : 25 * mm});
        }
    });
